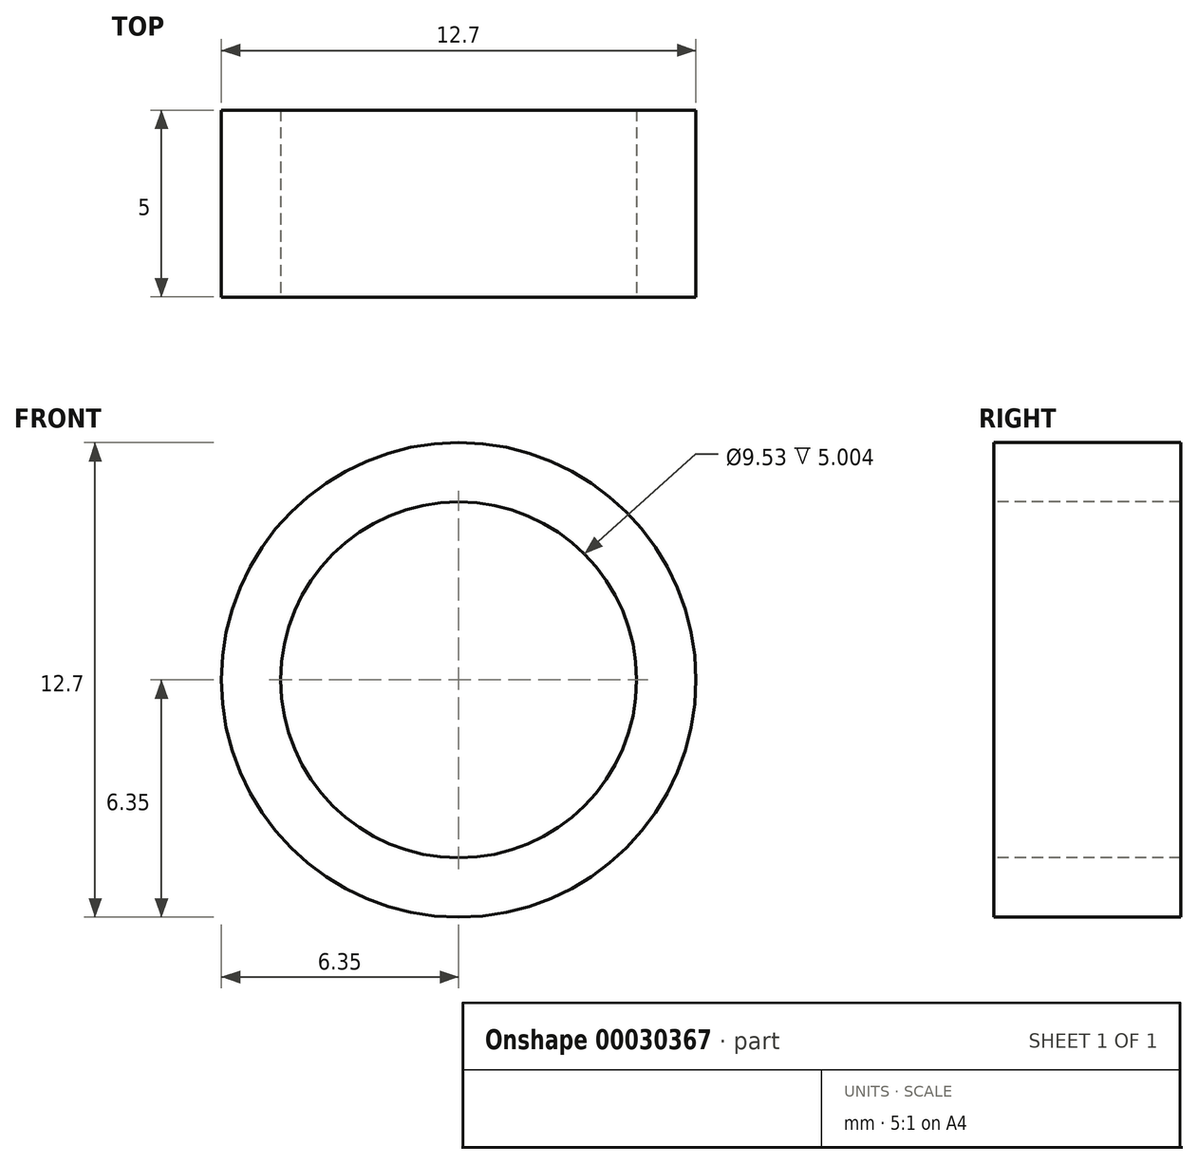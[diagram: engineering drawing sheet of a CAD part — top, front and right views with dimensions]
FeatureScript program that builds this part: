
annotation { "Feature Type Name" : "Feature", "Feature Type Description" : "" }
export const myFeature = defineFeature(function(context is Context, id is Id, definition is map)
    precondition{}
    {
        {
            var Q0;
            Q0=qCreatedBy(makeId("Front.planeOp"),FACE);
            var sketch = newSketch(context, id + "F0", { "sketchPlane" : qUnion([Q0])});
            skCircle(sketch, "E0", {"center": v(0, 0) * mm, "radius": 6.35 * mm});
            skSolve(sketch);
        }
        {
            var Q0;
            Q0 = qSketchRegion(id + "F0", true);
            extrude(context, id + "F1", {"entities" : qUnion([Q0]), "depth" : 5 * mm});
        }
        {
            var Q0;
            Q0=makeQuery(id+"F1.opExtrude","CAP_FACE",FACE,{"disambiguationData":[OSD([sQuery(id+"F0.wireOp",EDGE,"E0")])],"isStart":false});
            var sketch = newSketch(context, id + "F2", { "sketchPlane" : qUnion([Q0])});
            skPoint(sketch, "E1", {"position": v(0, 0) * mm});
            skSolve(sketch);
        }
        {
            var Q0;
            Q0=sQuery(id+"F2.wireOp",VERTEX,"E1");
            var Q1;
            Q1=makeQuery(id+"F1.opExtrude","SWEPT_BODY",BODY,{"disambiguationData":[OSD([sQuery(id+"F0.wireOp",EDGE,"E0")])]});
            hole(context, id + "F3", {"style" : HoleStyle.SIMPLE, "holeDiameter" : 9.52 * mm, "endStyle" : HoleEndStyle.THROUGH, "locations" : qUnion([Q0]), "scope" : qUnion([Q1])});
        }
    });
